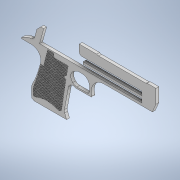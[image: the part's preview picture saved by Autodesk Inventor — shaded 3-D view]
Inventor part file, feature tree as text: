
AUTODESK INVENTOR PART (.ipt)
format: ipt  version: 2022 (Build 260153000, 153)  size: 7,829,504 bytes
history: native  units: in
note: dims shown in document units (in); Inventor stores cm internally (conversion verified against a paired STEP export)
features: sketch x8, other x8, extrude x3, reference x2, sheet_metal_op x1, plane x1, mirror x1, projected_geometry x1
ambient origin geometry x8: Origin, YZ Plane, XZ Plane, XY Plane, X Axis, Y Axis, Z Axis, Center Point
bodies: Body1 (feature_tree)
feature tree (25):
  sketch  "Sketch5"  dims[d104=0.0in]
  sketch  "Sketch3"  dims[d93=0.2333in d94=3.0666in]
  sketch  "Sketch2"  dims[d25=2.7559in d87=0.2234in]
  sheet_metal_op  "Face3"
  extrude  "Extrusion1"  Depth=0.2234in
  extrude  "Extrusion2"  Depth=3.0666in
  extrude  "Extrusion3"  Depth=0.0591in
  plane  "Work Plane1"
  mirror  "Mirror1"
  other  "Image2"
  other  "Image3"
  sketch  "Sketch4"  dims[d99=0.0591in d103=0.0591in]
  other  "Image4"
  other  "Plate3"
  reference  "Reference1"
  reference  "Reference2"
  sketch  "Sketch7"  dims[d105=0.0039in d106=0.0in]
  sketch  "Sketch8"  dims[d107=0.0079in]
  sketch  "Sketch9"  dims[d108=0.0039in d109=0.0in]
  projected_geometry  "Projected Loop1"
  sketch  "Sketch10"  dims[d110=23.622in d112=0.0197in d113=0.3937in d115=0.3937in d117=45.0deg d119=23.622in d121=0.3937in d122=0.0079in d123=0.0295in d124=135.0deg d125=0.3937in d126=0.0039in d127=0.0in]
  other  "Cut1"
  parser-record x1  (decoder bookkeeping rows leaked as tree rows — omitted from the tree; the rows remain in map.json)
  other  "Assembly1.iam"
  other  "sheetmettaal_2:2"
note: 1 file-system path scrubbed to <path> (originals preserved in map.json)
